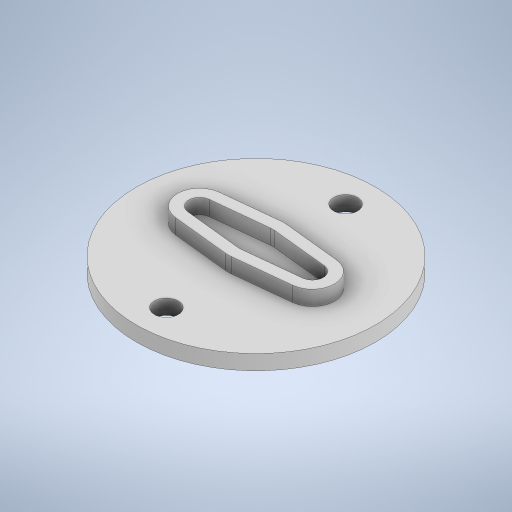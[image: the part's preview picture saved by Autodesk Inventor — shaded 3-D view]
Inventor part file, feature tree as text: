
AUTODESK INVENTOR PART (.ipt)
format: ipt  version: 2024 (Build 280153000, 153)  size: 285,184 bytes
history: native  units: in
note: dims shown in document units (in); Inventor stores cm internally (conversion verified against a paired STEP export)
features: extrude x2, sketch x2
ambient origin geometry x8: Origin, YZ Plane, XZ Plane, XY Plane, X Axis, Y Axis, Z Axis, Center Point
bodies: Solid1 (feature_tree)
feature tree (4):
  extrude  "Extrusion1"  Depth=0.2in
  extrude  "Extrusion2"  Depth=0.125in
  sketch  "Sketch1"  dims[d0=2.0in d1=0.2in]
  sketch  "Sketch2"  dims[d2=0.2in d3=1.5in d4=0.125in d5=0.0in d6=0.2165in d7=0.1181in d8=1.063in d9=0.0312in d10=0.0312in d11=0.0312in d12=0.0312in d13=0.0312in d14=0.0312in d15=0.0312in d16=0.0938in d17=0.0938in d18=0.0938in d19=0.0938in d20=0.0938in d21=0.0938in d22=0.0938in d23=0.125in d24=0.0in]
